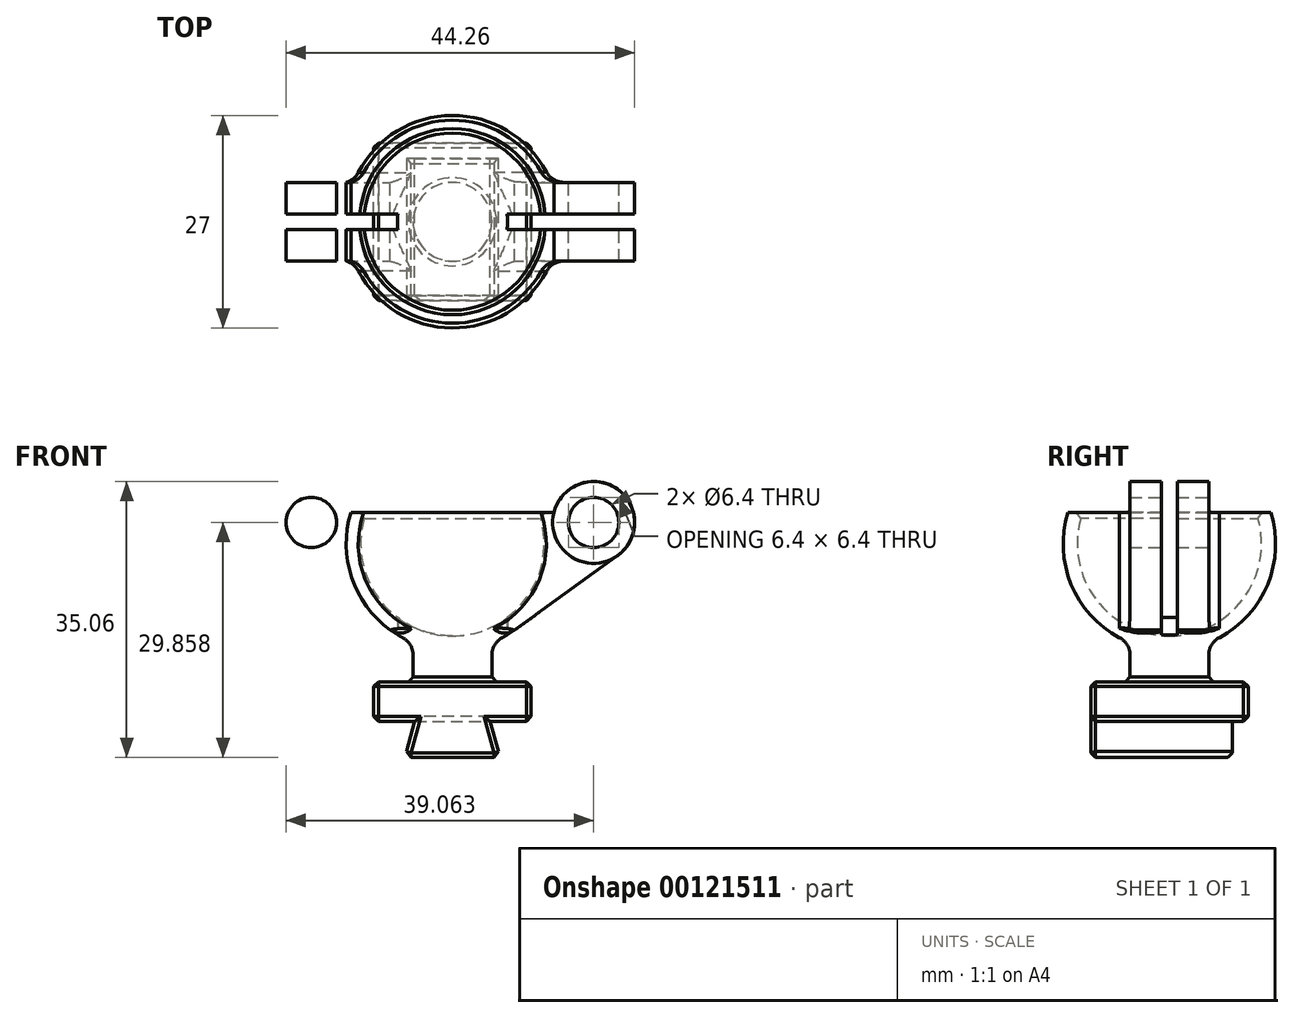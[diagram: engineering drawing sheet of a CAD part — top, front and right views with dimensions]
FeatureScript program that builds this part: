
annotation { "Feature Type Name" : "Feature", "Feature Type Description" : "" }
export const myFeature = defineFeature(function(context is Context, id is Id, definition is map)
    precondition{}
    {
        {
            assignVariable(context, id + "F0", {"name" : "BallWallThickness", "anyValue" : 2});
        }
        {
            assignVariable(context, id + "F1", {"name" : "DovetailBackstopDepth", "anyValue" : 2});
        }
        {
            assignVariable(context, id + "F2", {"name" : "DovetailHeight", "anyValue" : 5});
        }
        {
            assignVariable(context, id + "F3", {"name" : "Thickness", "anyValue" : 20});
        }
        {
            var Q0;
            Q0=qCreatedBy(makeId("Front.planeOp"),FACE);
            var sketch = newSketch(context, id + "F4", { "sketchPlane" : qUnion([Q0])});
            skLineSegment(sketch, "E0", {"start": v(20, 0) * mm, "end": v(20, 5) * mm});
            skLineSegment(sketch, "E1", {"start": v(20, 5) * mm, "end": v(0, 5) * mm});
            skLineSegment(sketch, "E2", {"start": v(5, 5) * mm, "end": v(5, 10) * mm});
            skLineSegment(sketch, "E3", {"start": v(5, 10) * mm, "end": v(15, 10) * mm});
            skLineSegment(sketch, "E4", {"start": v(15, 10) * mm, "end": v(15, 5) * mm});
            skLineSegment(sketch, "E5", {"start": v(10, 5) * mm, "end": v(10, -4.6) * mm, "construction": true});
            skArc(sketch, "E6", {"start": v(-2.9, 26.54) * mm, "mid": v(-2.18, 16.73) * mm, "end": v(5, 10) * mm});
            skPoint(sketch, "E6.centerSnap0", {"position": v(10, 10) * mm});
            skArc(sketch, "E7.trimOffspring", {"start": v(15, 10) * mm, "mid": v(22.18, 16.73) * mm, "end": v(22.9, 26.54) * mm});
            skLineSegment(sketch, "E8", {"start": v(10, 26.54) * mm, "end": v(10, 5) * mm});
            skArc(sketch, "E9", {"start": v(-1, 26.54) * mm, "mid": v(10, 10.84) * mm, "end": v(21, 26.54) * mm});
            skLineSegment(sketch, "E10", {"start": v(5.2, 0) * mm, "end": v(3.97, -4.6) * mm});
            skLineSegment(sketch, "E11", {"start": v(3.97, -4.6) * mm, "end": v(16.03, -4.6) * mm});
            skLineSegment(sketch, "E12.MirrorCS", {"start": v(14.8, 0) * mm, "end": v(16.03, -4.6) * mm});
            skLineSegment(sketch, "E13", {"start": v(14.8, 0) * mm, "end": v(20, 0) * mm});
            skLineSegment(sketch, "E14", {"start": v(5.2, 0) * mm, "end": v(0, 0) * mm});
            skLineSegment(sketch, "E15", {"start": v(0, 0) * mm, "end": v(0, 5) * mm});
            skLineSegment(sketch, "E16", {"start": v(-3.5, 22.54) * mm, "end": v(23.5, 22.54) * mm, "construction": true});
            skLineSegment(sketch, "E17", {"start": v(22.9, 26.54) * mm, "end": v(-2.9, 26.54) * mm});
            skLineSegment(sketch, "E18", {"start": v(5.2, 0) * mm, "end": v(14.8, 0) * mm});
            skCircle(sketch, "E19", {"center": v(27.93, 25.26) * mm, "radius": 3.2 * mm});
            skArc(sketch, "E20.0", {"start": v(30.98, 21.04) * mm, "mid": v(30.86, 29.56) * mm, "end": v(22.9, 26.54) * mm});
            skLineSegment(sketch, "E21", {"start": v(30.98, 21.04) * mm, "end": v(17.9, 11.6) * mm});
            skCircle(sketch, "E22.MirrorC", {"center": v(-7.93, 25.26) * mm, "radius": 3.2 * mm});
            skLineSegment(sketch, "E23.MirrorCS", {"start": v(-10.98, 21.04) * mm, "end": v(2.1, 11.6) * mm});
            skArc(sketch, "E24.MirrorCS", {"start": v(-10.98, 21.04) * mm, "mid": v(-10.86, 29.56) * mm, "end": v(-2.9, 26.54) * mm});
            skLineSegment(sketch, "E25", {"start": v(17.9, 11.6) * mm, "end": v(16.85, 13.06) * mm});
            skLineSegment(sketch, "E26.MirrorCS", {"start": v(2.1, 11.6) * mm, "end": v(3.15, 13.06) * mm});
            skSolve(sketch);
        }
        {
            var Q0;
            Q0=makeQuery(id+"F4.imprint","IMPRINT",FACE,{"disambiguationData":[TD([[makeQuery(id+"F4.imprint","IMPRINT",EDGE,{"derivedFrom":sQuery(id+"F4.wireOp",EDGE,"E10")}),1.0]])]});
            extrude(context, id + "F5", {"entities" : qUnion([Q0]), "depth" : (getVariable(context, 'Thickness') / 2) * mm, "hasSecondDirection" : true, "secondDirectionOppositeDirection" : true, "secondDirectionDepth" : (getVariable(context, 'Thickness') / 2 - getVariable(context, 'DovetailBackstopDepth')) * mm});
        }
        {
            var Q0;
            {var subQ4=sQuery(id+"F4.wireOp",EDGE,"E0");Q0=makeQuery(id+"F4.imprint","IMPRINT",FACE,{"disambiguationData":[TD([[makeQuery(id+"F4.imprint","IMPRINT",EDGE,{"derivedFrom":subQ4}),1.0]])]});}
            extrude(context, id + "F6", {"entities" : qUnion([Q0]), "operationType" : NewBodyOperationType.ADD, "endBound" : BoundingType.SYMMETRIC, "depth" : (getVariable(context, 'Thickness')) * mm});
        }
        {
            var Q0;
            {var subQ0=sQuery(id+"F4.wireOp",EDGE,"E2");Q0=makeQuery(id+"F4.imprint","IMPRINT",FACE,{"disambiguationData":[TD([[makeQuery(id+"F4.imprint","IMPRINT",EDGE,{"derivedFrom":subQ0}),-1.0]])]});}
            var Q1;
            Q1=sQuery(id+"F4.wireOp",EDGE,"E8");
            revolve(context, id + "F7", {"operationType" : NewBodyOperationType.ADD, "entities" : qUnion([Q0]), "axis" : qUnion([Q1]), "revolveType" : RevolveType.FULL});
        }
        {
            var Q0;
            Q0=makeQuery(id+"F7.opRevolve","SWEPT_FACE",FACE,{"disambiguationData":[OSD([sQuery(id+"F4.wireOp",EDGE,"E3")])]});
            var sketch = newSketch(context, id + "F8", { "sketchPlane" : qUnion([Q0])});
            skCircle(sketch, "E27", {"center": v(10, 0) * mm, "radius": 13.5 * mm});
            skCircle(sketch, "E28.0", {"center": v(10, 0) * mm, "radius": 5 * mm});
            skLineSegment(sketch, "E29", {"start": v(10, 13.5) * mm, "end": v(10, -13.5) * mm, "construction": true});
            skLineSegment(sketch, "E30", {"start": v(9.5, 13.5) * mm, "end": v(9.5, 6.98) * mm, "construction": true});
            skLineSegment(sketch, "E31.MirrorCS", {"start": v(10.5, 13.5) * mm, "end": v(10.5, 6.98) * mm, "construction": true});
            skLineSegment(sketch, "E32.trimOffspring", {"start": v(9.5, -6.98) * mm, "end": v(9.5, -13.5) * mm, "construction": true});
            skLineSegment(sketch, "E33.trimOffspring", {"start": v(10.5, -6.98) * mm, "end": v(10.5, -13.5) * mm, "construction": true});
            skLineSegment(sketch, "E34", {"start": v(-3.5, 0) * mm, "end": v(23.5, 0) * mm, "construction": true});
            skLineSegment(sketch, "E35", {"start": v(-3.46, 1) * mm, "end": v(3.07, 1) * mm});
            skLineSegment(sketch, "E36.MirrorCS", {"start": v(-3.46, -1) * mm, "end": v(3.07, -1) * mm});
            skLineSegment(sketch, "E37.trimOffspring", {"start": v(16.93, -1) * mm, "end": v(23.46, -1) * mm});
            skLineSegment(sketch, "E38.trimOffspring", {"start": v(16.93, 1) * mm, "end": v(23.46, 1) * mm});
            skCircle(sketch, "E39.0", {"center": v(10, 0) * mm, "radius": 7 * mm});
            skLineSegment(sketch, "E40", {"start": v(-3.46, -1) * mm, "end": v(-33.46, -1) * mm});
            skLineSegment(sketch, "E41", {"start": v(-33.46, -1) * mm, "end": v(-33.46, 1) * mm});
            skLineSegment(sketch, "E42", {"start": v(-33.46, 1) * mm, "end": v(-3.46, 1) * mm});
            skLineSegment(sketch, "E43.MirrorCS", {"start": v(53.46, 1) * mm, "end": v(23.46, 1) * mm});
            skLineSegment(sketch, "E44.MirrorCS", {"start": v(23.46, -1) * mm, "end": v(53.46, -1) * mm});
            skLineSegment(sketch, "E45.MirrorCS", {"start": v(53.46, -1) * mm, "end": v(53.46, 1) * mm});
            skSolve(sketch);
        }
        {
            var Q0;
            {var subQ6=sQuery(id+"F4.wireOp",EDGE,"E6");Q0=makeQuery(id+"F4.imprint","IMPRINT",FACE,{"disambiguationData":[TD([[makeQuery(id+"F4.imprint","IMPRINT",EDGE,{"derivedFrom":subQ6}),1.0]])]});}
            var Q1;
            {var subQ0=sQuery(id+"F4.wireOp",EDGE,"E26.MirrorCS");Q1=makeQuery(id+"F4.imprint","IMPRINT",FACE,{"disambiguationData":[TD([[makeQuery(id+"F4.imprint","IMPRINT",EDGE,{"derivedFrom":subQ0}),-1.0]])]});}
            var Q2;
            Q2=sQuery(id+"F4.wireOp",EDGE,"E8");
            revolve(context, id + "F9", {"operationType" : NewBodyOperationType.ADD, "entities" : qUnion([Q0, Q1]), "axis" : qUnion([Q2]), "revolveType" : RevolveType.FULL});
        }
        {
            var Q0;
            Q0=makeQuery(id+"F4.imprint","IMPRINT",FACE,{"disambiguationData":[TD([[makeQuery(id+"F4.imprint","IMPRINT",EDGE,{"derivedFrom":sQuery(id+"F4.wireOp",EDGE,"E22.MirrorC")}),1.0]])]});
            var Q1;
            {var subQ3=sQuery(id+"F4.wireOp",EDGE,"E26.MirrorCS");Q1=makeQuery(id+"F4.imprint","IMPRINT",FACE,{"disambiguationData":[TD([[makeQuery(id+"F4.imprint","IMPRINT",EDGE,{"derivedFrom":subQ3}),1.0]])]});}
            var Q2;
            {var subQ3=sQuery(id+"F4.wireOp",EDGE,"E25");Q2=makeQuery(id+"F4.imprint","IMPRINT",FACE,{"disambiguationData":[TD([[makeQuery(id+"F4.imprint","IMPRINT",EDGE,{"derivedFrom":subQ3}),-1.0]])]});}
            var Q3;
            Q3=makeQuery(id+"F4.imprint","IMPRINT",FACE,{"disambiguationData":[TD([[makeQuery(id+"F4.imprint","IMPRINT",EDGE,{"derivedFrom":sQuery(id+"F4.wireOp",EDGE,"E19")}),-1.0]])]});
            extrude(context, id + "F10", {"entities" : qUnion([Q0, Q1, Q2, Q3]), "operationType" : NewBodyOperationType.ADD, "endBound" : BoundingType.SYMMETRIC, "depth" : (getVariable(context, 'BallWallThickness') + 8) * mm});
        }
        {
            var Q0;
            {var subQ0=sQuery(id+"F8.wireOp",EDGE,"E35");Q0=makeQuery(id+"F8.imprint","IMPRINT",FACE,{"disambiguationData":[TD([[makeQuery(id+"F8.imprint","IMPRINT",EDGE,{"derivedFrom":subQ0}),-1.0]])]});}
            var Q1;
            {var subQ0=sQuery(id+"F8.wireOp",EDGE,"E32.trimOffspring");Q1=makeQuery(id+"F8.imprint","IMPRINT",FACE,{"disambiguationData":[TD([[makeQuery(id+"F8.imprint","IMPRINT",EDGE,{"derivedFrom":subQ0}),1.0]])]});}
            var Q2;
            {var subQ0=sQuery(id+"F8.wireOp",EDGE,"E37.trimOffspring");Q2=makeQuery(id+"F8.imprint","IMPRINT",FACE,{"disambiguationData":[TD([[makeQuery(id+"F8.imprint","IMPRINT",EDGE,{"derivedFrom":subQ0}),1.0]])]});}
            var Q3;
            {var subQ0=sQuery(id+"F8.wireOp",EDGE,"E30");Q3=makeQuery(id+"F8.imprint","IMPRINT",FACE,{"disambiguationData":[TD([[makeQuery(id+"F8.imprint","IMPRINT",EDGE,{"derivedFrom":subQ0}),1.0]])]});}
            var Q4;
            {var subQ2=sQuery(id+"F8.wireOp",EDGE,"E40");Q4=makeQuery(id+"F8.imprint","IMPRINT",FACE,{"disambiguationData":[TD([[makeQuery(id+"F8.imprint","IMPRINT",EDGE,{"derivedFrom":subQ2}),-1.0]])]});}
            var Q5;
            {var subQ2=sQuery(id+"F8.wireOp",EDGE,"E43.MirrorCS");Q5=makeQuery(id+"F8.imprint","IMPRINT",FACE,{"disambiguationData":[TD([[makeQuery(id+"F8.imprint","IMPRINT",EDGE,{"derivedFrom":subQ2}),1.0]])]});}
            extrude(context, id + "F11", {"entities" : qUnion([Q0, Q1, Q2, Q3, Q4, Q5]), "operationType" : NewBodyOperationType.REMOVE, "depth" : 25 * mm});
        }
        {
            var Q0;
            {var subQ0=sQuery(id+"F4.wireOp",EDGE,"E6");var subQ1=sQuery(id+"F4.wireOp",EDGE,"E3");var subQ2=sQuery(id+"F4.wireOp",EDGE,"E2");Q0=makeQuery(id+"F9.boolean.opBoolean","MERGE",EDGE,{"derivedFrom":[makeQuery(id+"F7.opRevolve","SWEPT_EDGE",EDGE,{"disambiguationData":[OSD([subQ2,subQ1,subQ0])]}),makeQuery(id+"F9.opRevolve","SWEPT_EDGE",EDGE,{"disambiguationData":[OSD([subQ2,subQ1,subQ0])]})]});}
            var Q1;
            Q1=makeQuery(id+"F7.opRevolve","SWEPT_EDGE",EDGE,{"disambiguationData":[OSD([sQuery(id+"F4.wireOp",EDGE,"E1"),sQuery(id+"F4.wireOp",EDGE,"E2")])]});
            var Q2;
            Q2=makeQuery(id+"F10.boolean.opBoolean","INTERSECT",EDGE,{"disambiguationData":[OD(1.0)],"derivedFrom":[makeQuery(id+"F9.opRevolve","SWEPT_FACE",FACE,{"disambiguationData":[OSD([sQuery(id+"F4.wireOp",EDGE,"E6")])]}),makeQuery(id+"F10.opExtrude","SWEPT_FACE",FACE,{"disambiguationData":[OSD([sQuery(id+"F4.wireOp",EDGE,"E26.MirrorCS")])]})]});
            var Q3;
            Q3=makeQuery(id+"F10.boolean.opBoolean","INTERSECT",EDGE,{"disambiguationData":[OD(1.0)],"derivedFrom":[makeQuery(id+"F9.opRevolve","SWEPT_FACE",FACE,{"disambiguationData":[OSD([sQuery(id+"F4.wireOp",EDGE,"E6")])]}),makeQuery(id+"F10.opExtrude","SWEPT_FACE",FACE,{"disambiguationData":[OSD([sQuery(id+"F4.wireOp",EDGE,"E25")])]})]});
            var Q4;
            Q4=makeQuery(id+"F10.boolean.opBoolean","INTERSECT",EDGE,{"disambiguationData":[OD(0.0)],"derivedFrom":[makeQuery(id+"F9.opRevolve","SWEPT_FACE",FACE,{"disambiguationData":[OSD([sQuery(id+"F4.wireOp",EDGE,"E6")])]}),makeQuery(id+"F10.opExtrude","SWEPT_FACE",FACE,{"disambiguationData":[OSD([sQuery(id+"F4.wireOp",EDGE,"E25")])]})]});
            var Q5;
            Q5=makeQuery(id+"F10.boolean.opBoolean","INTERSECT",EDGE,{"disambiguationData":[OD(0.0)],"derivedFrom":[makeQuery(id+"F9.opRevolve","SWEPT_FACE",FACE,{"disambiguationData":[OSD([sQuery(id+"F4.wireOp",EDGE,"E6")])]}),makeQuery(id+"F10.opExtrude","SWEPT_FACE",FACE,{"disambiguationData":[OSD([sQuery(id+"F4.wireOp",EDGE,"E26.MirrorCS")])]})]});
            var Q6;
            Q6=makeQuery(id+"F10.boolean.opBoolean","INTERSECT",EDGE,{"derivedFrom":[makeQuery(id+"F9.opRevolve","SWEPT_FACE",FACE,{"disambiguationData":[OSD([sQuery(id+"F4.wireOp",EDGE,"E6")])]}),makeQuery(id+"F10.opExtrude","CAP_FACE",FACE,{"disambiguationData":[OSD([sQuery(id+"F4.wireOp",EDGE,"E9"),sQuery(id+"F4.wireOp",EDGE,"E17"),sQuery(id+"F4.wireOp",EDGE,"E19"),sQuery(id+"F4.wireOp",EDGE,"E20.0"),sQuery(id+"F4.wireOp",EDGE,"E21"),sQuery(id+"F4.wireOp",EDGE,"E25")])],"isStart":false})]});
            var Q7;
            Q7=makeQuery(id+"F10.boolean.opBoolean","INTERSECT",EDGE,{"derivedFrom":[makeQuery(id+"F9.opRevolve","SWEPT_FACE",FACE,{"disambiguationData":[OSD([sQuery(id+"F4.wireOp",EDGE,"E6")])]}),makeQuery(id+"F10.opExtrude","CAP_FACE",FACE,{"disambiguationData":[OSD([sQuery(id+"F4.wireOp",EDGE,"E9"),sQuery(id+"F4.wireOp",EDGE,"E17"),sQuery(id+"F4.wireOp",EDGE,"E22.MirrorC"),sQuery(id+"F4.wireOp",EDGE,"E23.MirrorCS"),sQuery(id+"F4.wireOp",EDGE,"E24.MirrorCS"),sQuery(id+"F4.wireOp",EDGE,"E26.MirrorCS")])],"isStart":false})]});
            var Q8;
            Q8=makeQuery(id+"F10.boolean.opBoolean","INTERSECT",EDGE,{"derivedFrom":[makeQuery(id+"F9.opRevolve","SWEPT_FACE",FACE,{"disambiguationData":[OSD([sQuery(id+"F4.wireOp",EDGE,"E6")])]}),makeQuery(id+"F10.opExtrude","CAP_FACE",FACE,{"disambiguationData":[OSD([sQuery(id+"F4.wireOp",EDGE,"E9"),sQuery(id+"F4.wireOp",EDGE,"E17"),sQuery(id+"F4.wireOp",EDGE,"E22.MirrorC"),sQuery(id+"F4.wireOp",EDGE,"E23.MirrorCS"),sQuery(id+"F4.wireOp",EDGE,"E24.MirrorCS"),sQuery(id+"F4.wireOp",EDGE,"E26.MirrorCS")])],"isStart":true})]});
            var Q9;
            Q9=makeQuery(id+"F10.boolean.opBoolean","INTERSECT",EDGE,{"derivedFrom":[makeQuery(id+"F9.opRevolve","SWEPT_FACE",FACE,{"disambiguationData":[OSD([sQuery(id+"F4.wireOp",EDGE,"E6")])]}),makeQuery(id+"F10.opExtrude","CAP_FACE",FACE,{"disambiguationData":[OSD([sQuery(id+"F4.wireOp",EDGE,"E9"),sQuery(id+"F4.wireOp",EDGE,"E17"),sQuery(id+"F4.wireOp",EDGE,"E19"),sQuery(id+"F4.wireOp",EDGE,"E20.0"),sQuery(id+"F4.wireOp",EDGE,"E21"),sQuery(id+"F4.wireOp",EDGE,"E25")])],"isStart":true})]});
            fillet(context, id + "F12", {"entities" : qUnion([Q0, Q1, Q2, Q3, Q4, Q5, Q6, Q7, Q8, Q9]), "radius" : (getVariable(context, 'DovetailHeight') / 2) * mm, "tangentPropagation" : true, "allowEdgeOverflow" : false});
        }
        {
            var Q0;
            {var subQ0=sQuery(id+"F4.wireOp",EDGE,"E18");Q0=makeQuery(id+"F6.boolean.opBoolean","MERGE",FACE,{"derivedFrom":[makeQuery(id+"F5.opExtrude","CAP_FACE",FACE,{"disambiguationData":[OSD([sQuery(id+"F4.wireOp",EDGE,"E10"),sQuery(id+"F4.wireOp",EDGE,"E11"),sQuery(id+"F4.wireOp",EDGE,"E12.MirrorCS"),subQ0])],"isStart":false}),makeQuery(id+"F6.opExtrude","CAP_FACE",FACE,{"disambiguationData":[OSD([sQuery(id+"F4.wireOp",EDGE,"E0"),sQuery(id+"F4.wireOp",EDGE,"E1"),sQuery(id+"F4.wireOp",EDGE,"E13"),sQuery(id+"F4.wireOp",EDGE,"E14"),sQuery(id+"F4.wireOp",EDGE,"E15"),subQ0])],"isStart":false})]});}
            var Q1;
            Q1=makeQuery(id+"F6.opExtrude","SWEPT_FACE",FACE,{"disambiguationData":[OSD([sQuery(id+"F4.wireOp",EDGE,"E15")])]});
            var Q2;
            Q2=makeQuery(id+"F6.opExtrude","CAP_FACE",FACE,{"disambiguationData":[OSD([sQuery(id+"F4.wireOp",EDGE,"E0"),sQuery(id+"F4.wireOp",EDGE,"E1"),sQuery(id+"F4.wireOp",EDGE,"E13"),sQuery(id+"F4.wireOp",EDGE,"E14"),sQuery(id+"F4.wireOp",EDGE,"E15"),sQuery(id+"F4.wireOp",EDGE,"E18")])],"isStart":true});
            var Q3;
            Q3=makeQuery(id+"F6.opExtrude","SWEPT_FACE",FACE,{"disambiguationData":[OSD([sQuery(id+"F4.wireOp",EDGE,"E0")])]});
            var Q4;
            Q4=makeQuery(id+"F5.opExtrude","SWEPT_FACE",FACE,{"disambiguationData":[OSD([sQuery(id+"F4.wireOp",EDGE,"E11")])]});
            var Q5;
            Q5=makeQuery(id+"F6.opExtrude","SWEPT_FACE",FACE,{"disambiguationData":[OSD([sQuery(id+"F4.wireOp",EDGE,"E1")])]});
            var Q6;
            {var subQ0=sQuery(id+"F4.wireOp",EDGE,"E9");var subQ1=sQuery(id+"F4.wireOp",EDGE,"E17");Q6=makeQuery(id+"F11.boolean.opBoolean","SPLIT",EDGE,{"disambiguationData":[TD([makeQuery(id+"F11.opExtrude","SWEPT_FACE",FACE,{"disambiguationData":[OSD([sQuery(id+"F8.wireOp",EDGE,"E30")])]})])],"derivedFrom":makeQuery(id+"F9.opRevolve","SWEPT_EDGE",EDGE,{"disambiguationData":[OSD([subQ0,subQ1])]})});}
            var Q7;
            {var subQ0=sQuery(id+"F4.wireOp",EDGE,"E9");var subQ1=sQuery(id+"F4.wireOp",EDGE,"E17");Q7=makeQuery(id+"F11.boolean.opBoolean","SPLIT",EDGE,{"disambiguationData":[TD([makeQuery(id+"F11.opExtrude","SWEPT_FACE",FACE,{"disambiguationData":[OSD([sQuery(id+"F8.wireOp",EDGE,"E32.trimOffspring")])]})])],"derivedFrom":makeQuery(id+"F9.opRevolve","SWEPT_EDGE",EDGE,{"disambiguationData":[OSD([subQ0,subQ1])]})});}
            var Q8;
            {var subQ0=sQuery(id+"F4.wireOp",EDGE,"E9");var subQ1=sQuery(id+"F4.wireOp",EDGE,"E17");Q8=makeQuery(id+"F11.boolean.opBoolean","SPLIT",EDGE,{"disambiguationData":[TD([makeQuery(id+"F11.opExtrude","SWEPT_FACE",FACE,{"disambiguationData":[OSD([sQuery(id+"F8.wireOp",EDGE,"E33.trimOffspring")])]})])],"derivedFrom":makeQuery(id+"F9.opRevolve","SWEPT_EDGE",EDGE,{"disambiguationData":[OSD([subQ0,subQ1])]})});}
            var Q9;
            {var subQ0=sQuery(id+"F4.wireOp",EDGE,"E9");var subQ1=sQuery(id+"F4.wireOp",EDGE,"E17");Q9=makeQuery(id+"F11.boolean.opBoolean","SPLIT",EDGE,{"disambiguationData":[TD([makeQuery(id+"F11.opExtrude","SWEPT_FACE",FACE,{"disambiguationData":[OSD([sQuery(id+"F8.wireOp",EDGE,"E31.MirrorCS")])]})])],"derivedFrom":makeQuery(id+"F9.opRevolve","SWEPT_EDGE",EDGE,{"disambiguationData":[OSD([subQ0,subQ1])]})});}
            var Q10;
            {var subQ0=sQuery(id+"F4.wireOp",EDGE,"E17");var subQ1=sQuery(id+"F4.wireOp",EDGE,"E9");Q10=makeQuery(id+"F11.boolean.opBoolean","SPLIT",EDGE,{"disambiguationData":[TD([makeQuery(id+"F11.opExtrude","SWEPT_FACE",FACE,{"disambiguationData":[OSD([sQuery(id+"F8.wireOp",EDGE,"E36.MirrorCS"),sQuery(id+"F8.wireOp",EDGE,"E40")])]})])],"derivedFrom":makeQuery(id+"F9.opRevolve","SWEPT_EDGE",EDGE,{"disambiguationData":[OSD([subQ1,subQ0])]})});}
            var Q11;
            {var subQ0=sQuery(id+"F4.wireOp",EDGE,"E17");var subQ1=sQuery(id+"F4.wireOp",EDGE,"E9");Q11=makeQuery(id+"F11.boolean.opBoolean","SPLIT",EDGE,{"disambiguationData":[TD([makeQuery(id+"F11.opExtrude","SWEPT_FACE",FACE,{"disambiguationData":[OSD([sQuery(id+"F8.wireOp",EDGE,"E35"),sQuery(id+"F8.wireOp",EDGE,"E42")])]})])],"derivedFrom":makeQuery(id+"F9.opRevolve","SWEPT_EDGE",EDGE,{"disambiguationData":[OSD([subQ1,subQ0])]})});}
            chamfer(context, id + "F13", {"entities" : qUnion([Q0, Q1, Q2, Q3, Q4, Q5, Q6, Q7, Q8, Q9, Q10, Q11]), "width" : 0.6 * mm, "tangentPropagation" : true});
        }
    });
